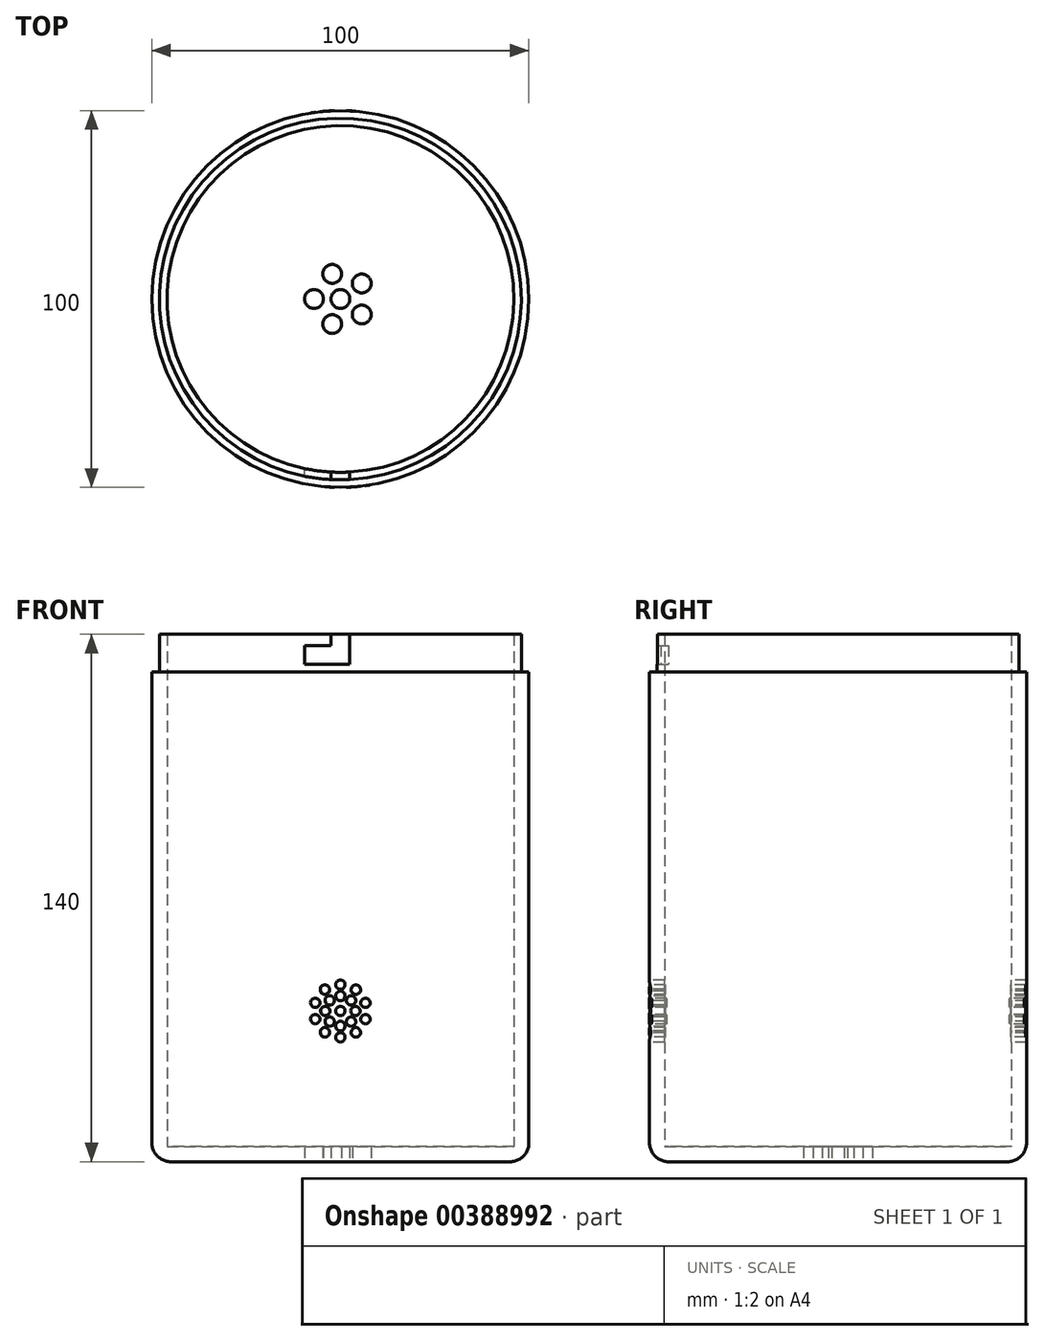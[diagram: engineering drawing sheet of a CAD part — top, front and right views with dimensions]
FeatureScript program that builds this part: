
annotation { "Feature Type Name" : "Feature", "Feature Type Description" : "" }
export const myFeature = defineFeature(function(context is Context, id is Id, definition is map)
    precondition{}
    {
        {
            var Q0;
            Q0=qCreatedBy(makeId("Top.planeOp"),FACE);
            var sketch = newSketch(context, id + "F0", { "sketchPlane" : qUnion([Q0])});
            skCircle(sketch, "E0", {"center": v(0, 0) * mm, "radius": 50 * mm});
            skCircle(sketch, "E1", {"center": v(0, 0) * mm, "radius": 2.5 * mm});
            skCircle(sketch, "E2", {"center": v(-7, 0) * mm, "radius": 2.5 * mm});
            skLineSegment(sketch, "E3", {"start": v(0, 0) * mm, "end": v(-50, 0) * mm, "construction": true});
            skCircle(sketch, "E4.1.0", {"center": v(-2.16, -6.66) * mm, "radius": 2.5 * mm});
            skCircle(sketch, "E4.2.0", {"center": v(5.66, -4.11) * mm, "radius": 2.5 * mm});
            skCircle(sketch, "E4.3.0", {"center": v(5.66, 4.11) * mm, "radius": 2.5 * mm});
            skCircle(sketch, "E4.4.0", {"center": v(-2.16, 6.66) * mm, "radius": 2.5 * mm});
            skSolve(sketch);
        }
        {
            var Q0;
            Q0=makeQuery(id+"F0.imprint","IMPRINT",FACE,{"disambiguationData":[TD([[makeQuery(id+"F0.imprint","IMPRINT",EDGE,{"derivedFrom":sQuery(id+"F0.wireOp",EDGE,"E0")}),1.0]])]});
            var Q1;
            Q1=makeQuery(id+"F0.imprint","IMPRINT",FACE,{"disambiguationData":[TD([[makeQuery(id+"F0.imprint","IMPRINT",EDGE,{"derivedFrom":sQuery(id+"F0.wireOp",EDGE,"E4.1.0")}),1.0]])]});
            var Q2;
            Q2=makeQuery(id+"F0.imprint","IMPRINT",FACE,{"disambiguationData":[TD([[makeQuery(id+"F0.imprint","IMPRINT",EDGE,{"derivedFrom":sQuery(id+"F0.wireOp",EDGE,"E4.2.0")}),1.0]])]});
            var Q3;
            Q3=makeQuery(id+"F0.imprint","IMPRINT",FACE,{"disambiguationData":[TD([[makeQuery(id+"F0.imprint","IMPRINT",EDGE,{"derivedFrom":sQuery(id+"F0.wireOp",EDGE,"E4.3.0")}),1.0]])]});
            var Q4;
            Q4=makeQuery(id+"F0.imprint","IMPRINT",FACE,{"disambiguationData":[TD([[makeQuery(id+"F0.imprint","IMPRINT",EDGE,{"derivedFrom":sQuery(id+"F0.wireOp",EDGE,"E1")}),1.0]])]});
            var Q5;
            Q5=makeQuery(id+"F0.imprint","IMPRINT",FACE,{"disambiguationData":[TD([[makeQuery(id+"F0.imprint","IMPRINT",EDGE,{"derivedFrom":sQuery(id+"F0.wireOp",EDGE,"E2")}),1.0]])]});
            var Q6;
            Q6=makeQuery(id+"F0.imprint","IMPRINT",FACE,{"disambiguationData":[TD([[makeQuery(id+"F0.imprint","IMPRINT",EDGE,{"derivedFrom":sQuery(id+"F0.wireOp",EDGE,"E4.4.0")}),1.0]])]});
            extrude(context, id + "F1", {"entities" : qUnion([Q0, Q1, Q2, Q3, Q4, Q5, Q6]), "depth" : 130 * mm});
        }
        {
            var Q0;
            Q0=makeQuery(id+"F1.opExtrude","CAP_FACE",FACE,{"disambiguationData":[OSD([sQuery(id+"F0.wireOp",EDGE,"E0")])],"isStart":false});
            shell(context, id + "F2", {"entities" : qUnion([Q0]), "thickness" : 4 * mm});
        }
        {
            var Q0;
            Q0=makeQuery(id+"F1.opExtrude","CAP_FACE",FACE,{"disambiguationData":[OSD([sQuery(id+"F0.wireOp",EDGE,"E0")])],"isStart":true});
            fillet(context, id + "F3", {"entities" : qUnion([Q0]), "radius" : 5 * mm, "tangentPropagation" : true, "allowEdgeOverflow" : false});
        }
        {
            var Q0;
            Q0=makeQuery(id+"F0.imprint","IMPRINT",FACE,{"disambiguationData":[TD([[makeQuery(id+"F0.imprint","IMPRINT",EDGE,{"derivedFrom":sQuery(id+"F0.wireOp",EDGE,"E4.2.0")}),1.0]])]});
            var Q1;
            Q1=makeQuery(id+"F0.imprint","IMPRINT",FACE,{"disambiguationData":[TD([[makeQuery(id+"F0.imprint","IMPRINT",EDGE,{"derivedFrom":sQuery(id+"F0.wireOp",EDGE,"E4.1.0")}),1.0]])]});
            var Q2;
            Q2=makeQuery(id+"F0.imprint","IMPRINT",FACE,{"disambiguationData":[TD([[makeQuery(id+"F0.imprint","IMPRINT",EDGE,{"derivedFrom":sQuery(id+"F0.wireOp",EDGE,"E1")}),1.0]])]});
            var Q3;
            Q3=makeQuery(id+"F0.imprint","IMPRINT",FACE,{"disambiguationData":[TD([[makeQuery(id+"F0.imprint","IMPRINT",EDGE,{"derivedFrom":sQuery(id+"F0.wireOp",EDGE,"E4.4.0")}),1.0]])]});
            var Q4;
            Q4=makeQuery(id+"F0.imprint","IMPRINT",FACE,{"disambiguationData":[TD([[makeQuery(id+"F0.imprint","IMPRINT",EDGE,{"derivedFrom":sQuery(id+"F0.wireOp",EDGE,"E4.3.0")}),1.0]])]});
            var Q5;
            Q5=makeQuery(id+"F0.imprint","IMPRINT",FACE,{"disambiguationData":[TD([[makeQuery(id+"F0.imprint","IMPRINT",EDGE,{"derivedFrom":sQuery(id+"F0.wireOp",EDGE,"E2")}),1.0]])]});
            extrude(context, id + "F4", {"entities" : qUnion([Q0, Q1, Q2, Q3, Q4, Q5]), "operationType" : NewBodyOperationType.REMOVE, "endBound" : BoundingType.THROUGH_ALL, "depth" : 25 * mm});
        }
        {
            var Q0;
            Q0=makeQuery(id+"F1.opExtrude","CAP_FACE",FACE,{"disambiguationData":[OSD([sQuery(id+"F0.wireOp",EDGE,"E0")])],"isStart":false});
            var sketch = newSketch(context, id + "F5", { "sketchPlane" : qUnion([Q0])});
            skCircle(sketch, "E5.0.0", {"center": v(0, 0) * mm, "radius": 50 * mm});
            skCircle(sketch, "E6.0", {"center": v(0, 0) * mm, "radius": 46 * mm});
            skCircle(sketch, "E7", {"center": v(0, 0) * mm, "radius": 48 * mm});
            skSolve(sketch);
        }
        {
            var Q0;
            Q0=makeQuery(id+"F5.imprint","IMPRINT",FACE,{"disambiguationData":[TD([[makeQuery(id+"F5.imprint","IMPRINT",EDGE,{"derivedFrom":sQuery(id+"F5.wireOp",EDGE,"E6.0")}),-1.0]])]});
            extrude(context, id + "F6", {"entities" : qUnion([Q0]), "operationType" : NewBodyOperationType.ADD, "depth" : 10 * mm});
        }
        {
            var Q0;
            Q0=qCreatedBy(makeId("Front.planeOp"),FACE);
            var sketch = newSketch(context, id + "F7", { "sketchPlane" : qUnion([Q0])});
            skLineSegment(sketch, "E8", {"start": v(-48, 120) * mm, "end": v(-48, 130) * mm});
            skLineSegment(sketch, "E9", {"start": v(48, 130) * mm, "end": v(48, 120) * mm});
            skLineSegment(sketch, "E10.0", {"start": v(-48, 140) * mm, "end": v(48, 140) * mm});
            skLineSegment(sketch, "E11.0", {"start": v(-48, 130) * mm, "end": v(48, 130) * mm});
            skPoint(sketch, "E12.middle", {"position": v(0, 140) * mm});
            skLineSegment(sketch, "E13.bottom", {"start": v(-2.5, 132) * mm, "end": v(-9.5, 132) * mm});
            skLineSegment(sketch, "E13.top", {"start": v(-2.5, 137) * mm, "end": v(-9.5, 137) * mm});
            skLineSegment(sketch, "E13.left", {"start": v(-2.5, 132) * mm, "end": v(-2.5, 137) * mm});
            skLineSegment(sketch, "E13.right", {"start": v(-9.5, 132) * mm, "end": v(-9.5, 137) * mm});
            skLineSegment(sketch, "E14.bottom", {"start": v(-2.5, 132) * mm, "end": v(2.5, 132) * mm});
            skLineSegment(sketch, "E14.top", {"start": v(-2.5, 148) * mm, "end": v(2.5, 148) * mm});
            skLineSegment(sketch, "E14.left", {"start": v(-2.5, 132) * mm, "end": v(-2.5, 148) * mm});
            skLineSegment(sketch, "E14.right", {"start": v(2.5, 132) * mm, "end": v(2.5, 148) * mm});
            skSolve(sketch);
        }
        {
            var Q0;
            {var subQ0=sQuery(id+"F7.wireOp",EDGE,"E13.bottom");Q0=makeQuery(id+"F7.imprint","IMPRINT",FACE,{"disambiguationData":[TD([[makeQuery(id+"F7.imprint","IMPRINT",EDGE,{"derivedFrom":subQ0}),-1.0]])]});}
            var Q1;
            {var subQ4=sQuery(id+"F7.wireOp",EDGE,"E14.bottom");Q1=makeQuery(id+"F7.imprint","IMPRINT",FACE,{"disambiguationData":[TD([[makeQuery(id+"F7.imprint","IMPRINT",EDGE,{"derivedFrom":subQ4}),1.0]])]});}
            extrude(context, id + "F8", {"entities" : qUnion([Q0, Q1]), "operationType" : NewBodyOperationType.REMOVE, "endBound" : BoundingType.THROUGH_ALL, "depth" : 25 * mm});
        }
        {
            var Q0;
            Q0=qCreatedBy(makeId("Front.planeOp"),FACE);
            var sketch = newSketch(context, id + "F9", { "sketchPlane" : qUnion([Q0])});
            skCircle(sketch, "E15", {"center": v(0, 40) * mm, "radius": 1.25 * mm});
            skCircle(sketch, "E16", {"center": v(0, 44) * mm, "radius": 1.25 * mm});
            skCircle(sketch, "E17.1.0", {"center": v(-2.83, 42.83) * mm, "radius": 1.25 * mm});
            skCircle(sketch, "E17.2.0", {"center": v(-4, 40) * mm, "radius": 1.25 * mm});
            skCircle(sketch, "E17.3.0", {"center": v(-2.83, 37.17) * mm, "radius": 1.25 * mm});
            skCircle(sketch, "E17.4.0", {"center": v(0, 36) * mm, "radius": 1.25 * mm});
            skCircle(sketch, "E17.5.0", {"center": v(2.83, 37.17) * mm, "radius": 1.25 * mm});
            skCircle(sketch, "E18.1.6.0", {"center": v(4, 40) * mm, "radius": 1.25 * mm});
            skCircle(sketch, "E18.1.7.0", {"center": v(2.83, 42.83) * mm, "radius": 1.25 * mm});
            skCircle(sketch, "E19", {"center": v(0, 47) * mm, "radius": 1.25 * mm});
            skCircle(sketch, "E20.1.0", {"center": v(-4.11, 45.66) * mm, "radius": 1.25 * mm});
            skCircle(sketch, "E20.2.0", {"center": v(-6.66, 42.16) * mm, "radius": 1.25 * mm});
            skCircle(sketch, "E20.3.0", {"center": v(-6.66, 37.84) * mm, "radius": 1.25 * mm});
            skCircle(sketch, "E20.4.0", {"center": v(-4.11, 34.34) * mm, "radius": 1.25 * mm});
            skCircle(sketch, "E20.5.0", {"center": v(0, 33) * mm, "radius": 1.25 * mm});
            skCircle(sketch, "E20.6.0", {"center": v(4.11, 34.34) * mm, "radius": 1.25 * mm});
            skCircle(sketch, "E20.7.0", {"center": v(6.66, 37.84) * mm, "radius": 1.25 * mm});
            skCircle(sketch, "E20.8.0", {"center": v(6.66, 42.16) * mm, "radius": 1.25 * mm});
            skCircle(sketch, "E20.9.0", {"center": v(4.11, 45.66) * mm, "radius": 1.25 * mm});
            skSolve(sketch);
        }
        {
            var Q0;
            Q0=qSketchRegion(id+"F9",true);
            extrude(context, id + "F10", {"entities" : qUnion([Q0]), "operationType" : NewBodyOperationType.REMOVE, "endBound" : BoundingType.THROUGH_ALL, "oppositeDirection" : true, "depth" : 25 * mm, "hasSecondDirection" : true, "secondDirectionBound" : SecondDirectionBoundingType.THROUGH_ALL, "secondDirectionOppositeDirection" : false, "secondDirectionDepth" : 25 * mm});
        }
    });
